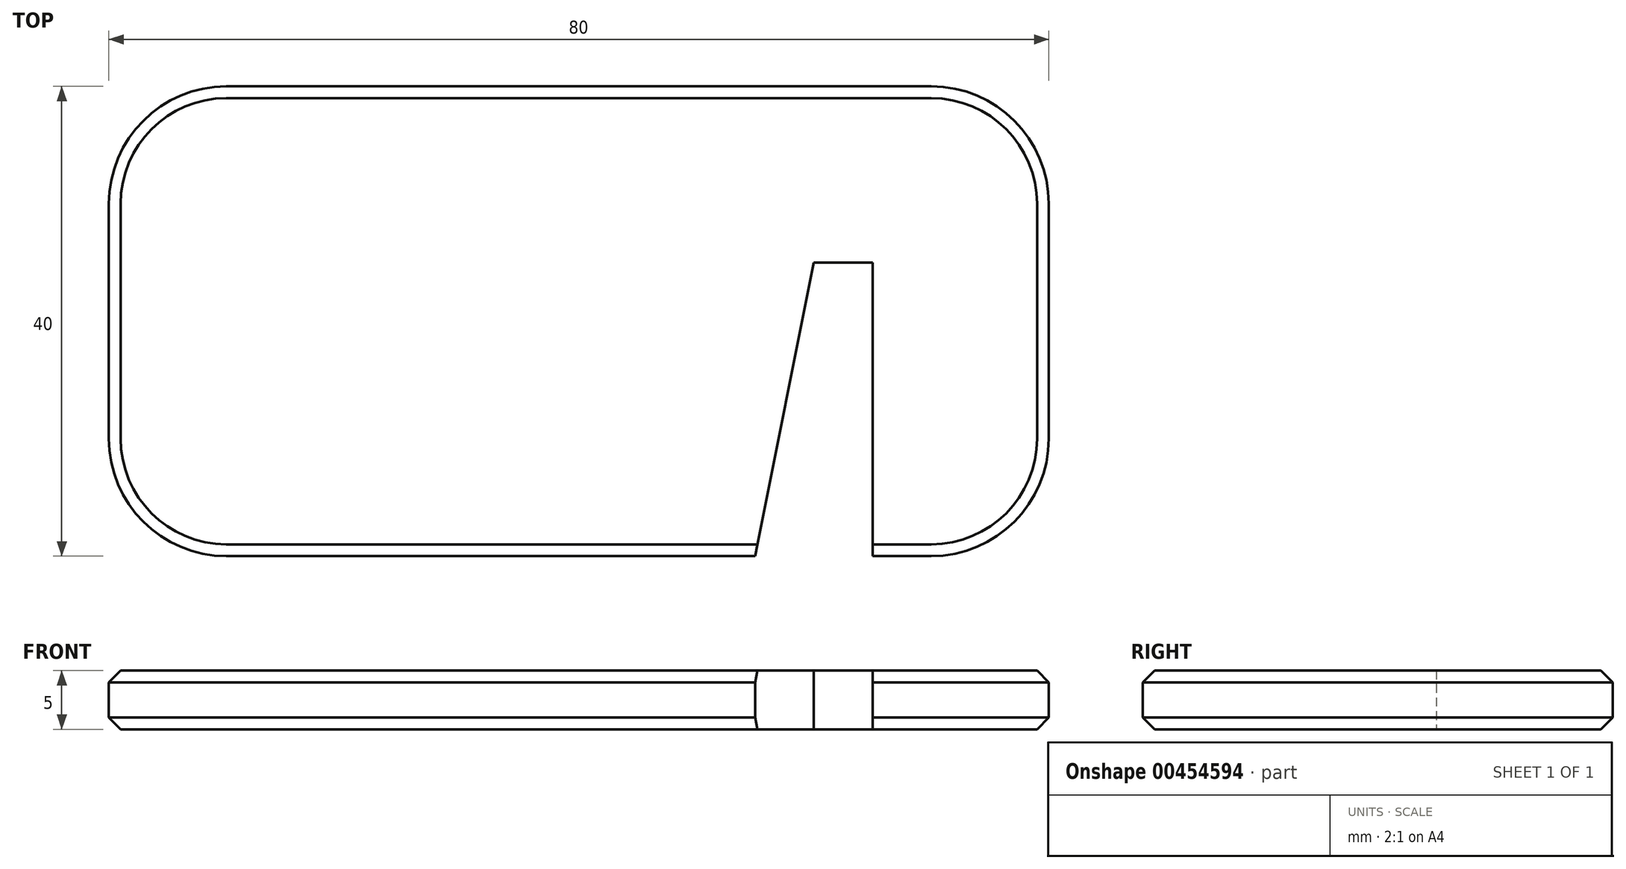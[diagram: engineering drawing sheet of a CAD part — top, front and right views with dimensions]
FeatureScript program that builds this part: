
annotation { "Feature Type Name" : "Feature", "Feature Type Description" : "" }
export const myFeature = defineFeature(function(context is Context, id is Id, definition is map)
    precondition{}
    {
        {
            var Q0;
            Q0=qCreatedBy(makeId("Top.planeOp"),FACE);
            var sketch = newSketch(context, id + "F0", { "sketchPlane" : qUnion([Q0])});
            skLineSegment(sketch, "E0.bottom", {"start": v(0, 0) * mm, "end": v(55, 0) * mm});
            skLineSegment(sketch, "E0.top", {"start": v(0, 40) * mm, "end": v(80, 40) * mm});
            skLineSegment(sketch, "E0.left", {"start": v(0, 0) * mm, "end": v(0, 40) * mm});
            skLineSegment(sketch, "E0.right", {"start": v(80, 0) * mm, "end": v(80, 40) * mm});
            skLineSegment(sketch, "E1", {"start": v(65, 0) * mm, "end": v(65, 25) * mm});
            skLineSegment(sketch, "E2", {"start": v(65, 25) * mm, "end": v(60, 25) * mm});
            skLineSegment(sketch, "E3", {"start": v(60, 25) * mm, "end": v(55, 0) * mm});
            skLineSegment(sketch, "E4.trimOffspring", {"start": v(65, 0) * mm, "end": v(80, 0) * mm});
            skSolve(sketch);
        }
        {
            var Q0;
            Q0=makeQuery(id+"F0.imprint","IMPRINT",FACE,{"disambiguationData":[TD([[makeQuery(id+"F0.imprint","IMPRINT",EDGE,{"derivedFrom":sQuery(id+"F0.wireOp",EDGE,"E0.bottom")}),1.0]])]});
            extrude(context, id + "F1", {"entities" : qUnion([Q0]), "depth" : 5 * mm});
        }
        {
            var Q0;
            Q0=makeQuery(id+"F1.opExtrude","SWEPT_EDGE",EDGE,{"disambiguationData":[OSD([sQuery(id+"F0.wireOp",EDGE,"E0.right"),sQuery(id+"F0.wireOp",EDGE,"E4.trimOffspring")])]});
            var Q1;
            Q1=makeQuery(id+"F1.opExtrude","SWEPT_EDGE",EDGE,{"disambiguationData":[OSD([sQuery(id+"F0.wireOp",EDGE,"E0.top"),sQuery(id+"F0.wireOp",EDGE,"E0.right")])]});
            var Q2;
            Q2=makeQuery(id+"F1.opExtrude","SWEPT_EDGE",EDGE,{"disambiguationData":[OSD([sQuery(id+"F0.wireOp",EDGE,"E0.top"),sQuery(id+"F0.wireOp",EDGE,"E0.left")])]});
            var Q3;
            Q3=makeQuery(id+"F1.opExtrude","SWEPT_EDGE",EDGE,{"disambiguationData":[OSD([sQuery(id+"F0.wireOp",EDGE,"E0.bottom"),sQuery(id+"F0.wireOp",EDGE,"E0.left")])]});
            fillet(context, id + "F2", {"entities" : qUnion([Q0, Q1, Q2, Q3]), "radius" : 10 * mm, "tangentPropagation" : true, "allowEdgeOverflow" : false});
        }
        {
            var Q0;
            {var subQ0=sQuery(id+"F0.wireOp",EDGE,"E4.trimOffspring");var subQ1=sQuery(id+"F0.wireOp",EDGE,"E0.right");Q0=makeQuery(id+"F2.opFillet","BLEND_EDGE",EDGE,{"blendedFrom":[makeQuery(id+"F1.opExtrude","SWEPT_EDGE",EDGE,{"disambiguationData":[OSD([subQ1,subQ0])]}),makeQuery(id+"F1.opExtrude","CAP_FACE",FACE,{"disambiguationData":[OSD([sQuery(id+"F0.wireOp",EDGE,"E0.bottom"),sQuery(id+"F0.wireOp",EDGE,"E0.top"),sQuery(id+"F0.wireOp",EDGE,"E0.left"),subQ1,sQuery(id+"F0.wireOp",EDGE,"E1"),sQuery(id+"F0.wireOp",EDGE,"E2"),sQuery(id+"F0.wireOp",EDGE,"E3"),subQ0])],"isStart":false})],"blendedInto":[makeQuery(id+"F1.opExtrude","CAP_FACE",FACE,{"disambiguationData":[OSD([sQuery(id+"F0.wireOp",EDGE,"E0.bottom"),sQuery(id+"F0.wireOp",EDGE,"E0.top"),sQuery(id+"F0.wireOp",EDGE,"E0.left"),subQ1,sQuery(id+"F0.wireOp",EDGE,"E1"),sQuery(id+"F0.wireOp",EDGE,"E2"),sQuery(id+"F0.wireOp",EDGE,"E3"),subQ0])],"isStart":false})]});}
            var Q1;
            {var subQ0=sQuery(id+"F0.wireOp",EDGE,"E4.trimOffspring");var subQ1=sQuery(id+"F0.wireOp",EDGE,"E0.right");Q1=makeQuery(id+"F2.opFillet","BLEND_EDGE",EDGE,{"blendedFrom":[makeQuery(id+"F1.opExtrude","SWEPT_EDGE",EDGE,{"disambiguationData":[OSD([subQ1,subQ0])]}),makeQuery(id+"F1.opExtrude","CAP_FACE",FACE,{"disambiguationData":[OSD([sQuery(id+"F0.wireOp",EDGE,"E0.bottom"),sQuery(id+"F0.wireOp",EDGE,"E0.top"),sQuery(id+"F0.wireOp",EDGE,"E0.left"),subQ1,sQuery(id+"F0.wireOp",EDGE,"E1"),sQuery(id+"F0.wireOp",EDGE,"E2"),sQuery(id+"F0.wireOp",EDGE,"E3"),subQ0])],"isStart":true})],"blendedInto":[makeQuery(id+"F1.opExtrude","CAP_FACE",FACE,{"disambiguationData":[OSD([sQuery(id+"F0.wireOp",EDGE,"E0.bottom"),sQuery(id+"F0.wireOp",EDGE,"E0.top"),sQuery(id+"F0.wireOp",EDGE,"E0.left"),subQ1,sQuery(id+"F0.wireOp",EDGE,"E1"),sQuery(id+"F0.wireOp",EDGE,"E2"),sQuery(id+"F0.wireOp",EDGE,"E3"),subQ0])],"isStart":true})]});}
            chamfer(context, id + "F3", {"entities" : qUnion([Q0, Q1]), "width" : 1 * mm, "tangentPropagation" : true});
        }
    });
